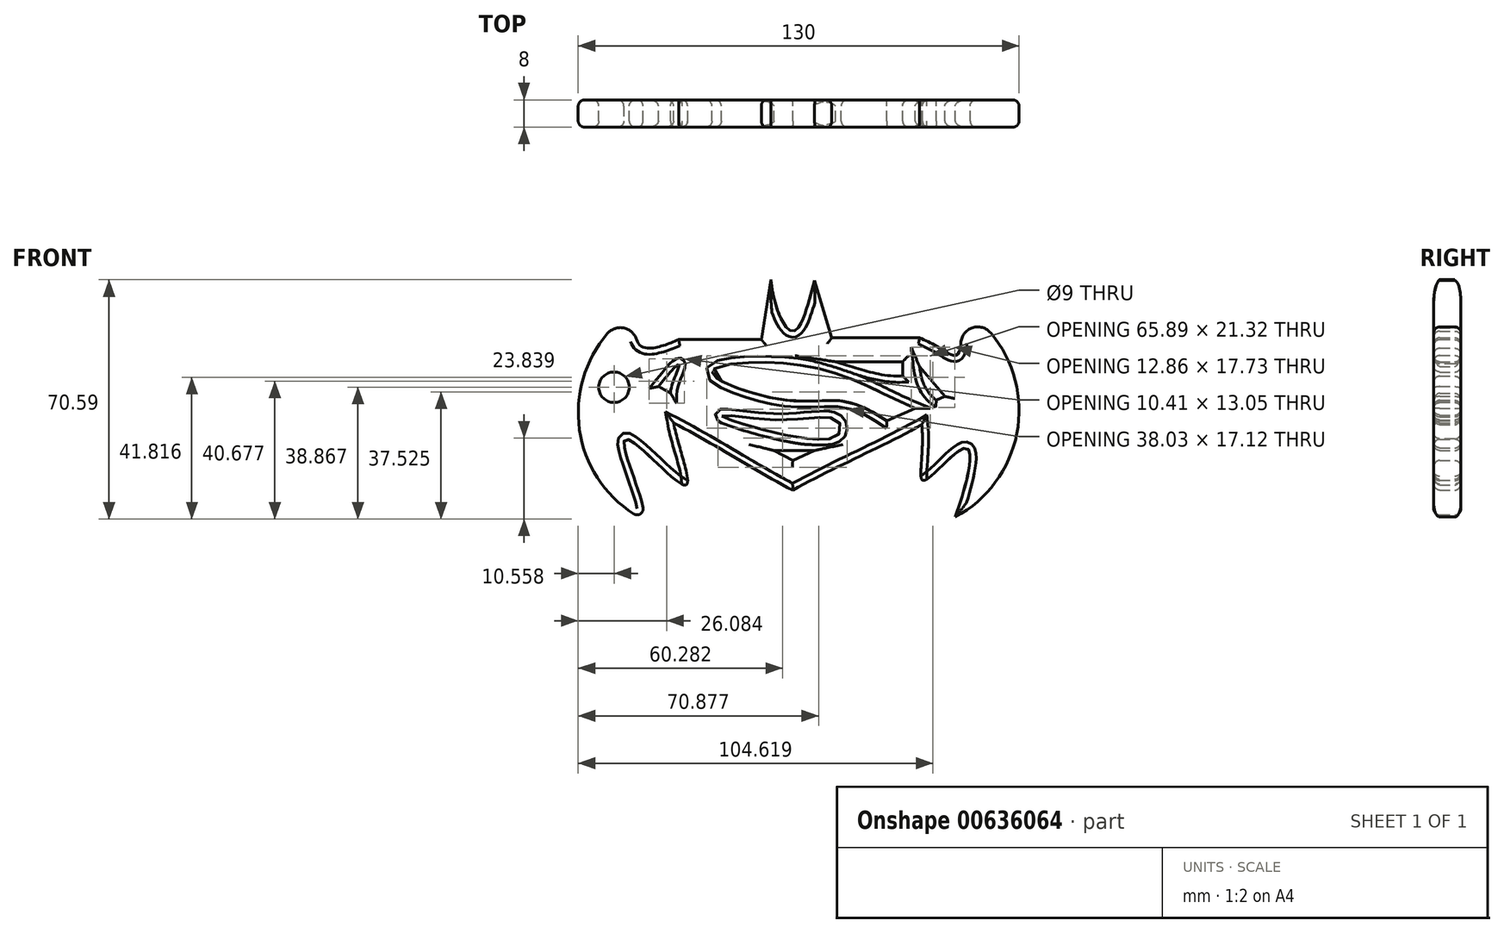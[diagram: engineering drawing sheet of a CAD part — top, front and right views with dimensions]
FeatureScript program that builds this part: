
annotation { "Feature Type Name" : "Feature", "Feature Type Description" : "" }
export const myFeature = defineFeature(function(context is Context, id is Id, definition is map)
    precondition{}
    {
        {
            var Q0;
            Q0=qCreatedBy(makeId("Front.planeOp"),FACE);
            var sketch = newSketch(context, id + "F0", { "sketchPlane" : qUnion([Q0])});
            skLineSegment(sketch, "E0", {"start": v(-12.91, 41.7) * mm, "end": v(-15.72, 24) * mm});
            skLineSegment(sketch, "E1", {"start": v(0, 41.41) * mm, "end": v(5.05, 24.57) * mm});
            skFitSpline(sketch, "E2", {"points": [v(-12.91, 41.7) * mm, v(-6.46, 26.53) * mm, v(0, 41.41) * mm], "startDerivative": vector(5.25, -48.76) * mm, "endDerivative": vector(12.88, 47.63) * mm});
            skLineSegment(sketch, "E3", {"start": v(-15.72, 24) * mm, "end": v(-40.11, 24) * mm});
            skLineSegment(sketch, "E4", {"start": v(5.05, 24.57) * mm, "end": v(30.98, 24.57) * mm});
            skFitSpline(sketch, "E5", {"points": [v(-40.11, 24) * mm, v(-51.3, 22.22) * mm, v(-50.91, 33.97) * mm], "startDerivative": vector(-39.59, -16.97) * mm, "endDerivative": vector(15.78, 44.08) * mm});
            skFitSpline(sketch, "E6", {"points": [v(30.98, 24.57) * mm, v(41.82, 19.47) * mm, v(41.48, 34.5) * mm], "startDerivative": vector(43.18, -18.5) * mm, "endDerivative": vector(-13.44, 48.11) * mm});
            skFitSpline(sketch, "E7", {"points": [v(41.48, -28.3) * mm, v(44.06, -8) * mm, v(32.34, -17.5) * mm, v(31.6, -1.1) * mm], "startDerivative": vector(35.63, 101) * mm, "endDerivative": vector(-8, 85.3) * mm});
            skFitSpline(sketch, "E8", {"points": [v(-50.91, -28.83) * mm, v(-50.91, -24.08) * mm, v(-55.7, -5.25) * mm, v(-38.31, -18.9) * mm, v(-41.58, -0.55) * mm], "startDerivative": vector(6.87, 19.6) * mm, "endDerivative": vector(-14.48, 80.7) * mm});
            skFitSpline(sketch, "E9", {"points": [v(-41.58, -0.55) * mm, v(-6.46, -20.38) * mm], "startDerivative": vector(37.07, -19.28) * mm, "endDerivative": vector(37.07, -19.28) * mm});
            skFitSpline(sketch, "E10", {"points": [v(31.6, -1.1) * mm, v(-6.46, -20.38) * mm], "startDerivative": vector(-37.45, -20.69) * mm, "endDerivative": vector(-37.45, -20.69) * mm});
            skLineSegment(sketch, "E11", {"start": v(-6.46, -15.44) * mm, "end": v(41.82, 6.41) * mm});
            skLineSegment(sketch, "E12", {"start": v(41.82, 6.41) * mm, "end": v(30.98, 21.66) * mm});
            skLineSegment(sketch, "E13", {"start": v(30.98, 21.66) * mm, "end": v(-40.11, 21.2) * mm});
            skLineSegment(sketch, "E14", {"start": v(-40.11, 21.2) * mm, "end": v(-51.3, 8.73) * mm});
            skLineSegment(sketch, "E15", {"start": v(-51.3, 8.73) * mm, "end": v(-6.46, -15.44) * mm});
            skArc(sketch, "E16", {"start": v(-50.91, 33.97) * mm, "mid": v(-69.72, 2.57) * mm, "end": v(-50.91, -28.83) * mm});
            skArc(sketch, "E17", {"start": v(41.48, -28.3) * mm, "mid": v(60.28, 3.1) * mm, "end": v(41.48, 34.5) * mm});
            skLineSegment(sketch, "E18", {"start": v(-6.46, -11.62) * mm, "end": v(0, -8.7) * mm});
            skLineSegment(sketch, "E19", {"start": v(0, -8.7) * mm, "end": v(-12.03, -8.7) * mm});
            skLineSegment(sketch, "E20", {"start": v(-12.03, -8.7) * mm, "end": v(-6.46, -11.62) * mm});
            skFitSpline(sketch, "E21", {"points": [v(-27.4, 1.5) * mm, v(-10.6, 0.35) * mm, v(6.93, 0) * mm, v(5.75, -4.85) * mm, v(-27.4, 1.5) * mm]});
            skLineSegment(sketch, "E22", {"start": v(-46.08, 10.16) * mm, "end": v(-42.51, 8.24) * mm});
            skLineSegment(sketch, "E23", {"start": v(35.92, 6.14) * mm, "end": v(38.41, 7.27) * mm});
            skLineSegment(sketch, "E24", {"start": v(38.41, 7.27) * mm, "end": v(30.96, 16.07) * mm});
            skFitSpline(sketch, "E25", {"points": [v(30.96, 16.07) * mm, v(35.92, 6.14) * mm], "startDerivative": vector(1.42, -12.05) * mm, "endDerivative": vector(10.63, -8.5) * mm});
            skLineSegment(sketch, "E26", {"start": v(25.93, 17.49) * mm, "end": v(25.96, 13.23) * mm});
            skLineSegment(sketch, "E27", {"start": v(25.96, 13.23) * mm, "end": v(25.93, 17.49) * mm});
            skLineSegment(sketch, "E28", {"start": v(6.14, 17.49) * mm, "end": v(25.93, 17.49) * mm});
            skFitSpline(sketch, "E29", {"points": [v(6.14, 17.49) * mm, v(25.96, 13.23) * mm], "startDerivative": vector(18.43, -5.67) * mm, "endDerivative": vector(19.75, 0.7) * mm});
            skLineSegment(sketch, "E30", {"start": v(21.34, 0) * mm, "end": v(29.64, 3.76) * mm});
            skFitSpline(sketch, "E31", {"points": [v(29.64, 3.76) * mm, v(-2.9, 16.3) * mm, v(-30.27, 14.52) * mm, v(-9.16, 6.26) * mm, v(8.78, 5.78) * mm, v(16.3, 3.13) * mm, v(21.34, 0) * mm], "startDerivative": vector(-155.46, 66.73) * mm, "endDerivative": vector(157.37, -97.92) * mm});
            skFitSpline(sketch, "E32", {"points": [v(-46.08, 10.16) * mm, v(-39.94, 16.69) * mm, v(-42.51, 8.24) * mm], "startDerivative": vector(16.59, 20.52) * mm, "endDerivative": vector(-0.25, -15.84) * mm});
            skCircle(sketch, "E33", {"center": v(-59.16, 9.97) * mm, "radius": 4.5 * mm});
            skSolve(sketch);
        }
        {
            var Q0;
            Q0=makeQuery(id+"F0.imprint","IMPRINT",FACE,{"disambiguationData":[TD([[makeQuery(id+"F0.imprint","IMPRINT",EDGE,{"derivedFrom":sQuery(id+"F0.wireOp",EDGE,"E11")}),1.0]])]});
            var Q1;
            Q1=makeQuery(id+"F0.imprint","IMPRINT",FACE,{"disambiguationData":[TD([[makeQuery(id+"F0.imprint","IMPRINT",EDGE,{"derivedFrom":sQuery(id+"F0.wireOp",EDGE,"E0")}),1.0]])]});
            extrude(context, id + "F1", {"entities" : qUnion([Q0, Q1]), "depth" : 8 * mm});
        }
        {
            var Q0;
            Q0=makeQuery(id+"F1.opExtrude","SWEPT_EDGE",EDGE,{"disambiguationData":[OSD([sQuery(id+"F0.wireOp",EDGE,"E8"),sQuery(id+"F0.wireOp",EDGE,"E16")])]});
            var Q1;
            Q1=makeQuery(id+"F1.opExtrude","CAP_FACE",FACE,{"disambiguationData":[OSD([sQuery(id+"F0.wireOp",EDGE,"E0"),sQuery(id+"F0.wireOp",EDGE,"E1"),sQuery(id+"F0.wireOp",EDGE,"E2"),sQuery(id+"F0.wireOp",EDGE,"E3"),sQuery(id+"F0.wireOp",EDGE,"E4"),sQuery(id+"F0.wireOp",EDGE,"E5"),sQuery(id+"F0.wireOp",EDGE,"E6"),sQuery(id+"F0.wireOp",EDGE,"E7"),sQuery(id+"F0.wireOp",EDGE,"E8"),sQuery(id+"F0.wireOp",EDGE,"E9"),sQuery(id+"F0.wireOp",EDGE,"E10"),sQuery(id+"F0.wireOp",EDGE,"E16"),sQuery(id+"F0.wireOp",EDGE,"E17"),sQuery(id+"F0.wireOp",EDGE,"E18"),sQuery(id+"F0.wireOp",EDGE,"E19"),sQuery(id+"F0.wireOp",EDGE,"E20"),sQuery(id+"F0.wireOp",EDGE,"E21"),sQuery(id+"F0.wireOp",EDGE,"E22"),sQuery(id+"F0.wireOp",EDGE,"E23"),sQuery(id+"F0.wireOp",EDGE,"E24"),sQuery(id+"F0.wireOp",EDGE,"E25"),sQuery(id+"F0.wireOp",EDGE,"E27"),sQuery(id+"F0.wireOp",EDGE,"E28"),sQuery(id+"F0.wireOp",EDGE,"E29"),sQuery(id+"F0.wireOp",EDGE,"E30"),sQuery(id+"F0.wireOp",EDGE,"E31"),sQuery(id+"F0.wireOp",EDGE,"E32"),sQuery(id+"F0.wireOp",EDGE,"E33")])],"isStart":true});
            var Q2;
            Q2=makeQuery(id+"F1.opExtrude","CAP_FACE",FACE,{"disambiguationData":[OSD([sQuery(id+"F0.wireOp",EDGE,"E0"),sQuery(id+"F0.wireOp",EDGE,"E1"),sQuery(id+"F0.wireOp",EDGE,"E2"),sQuery(id+"F0.wireOp",EDGE,"E3"),sQuery(id+"F0.wireOp",EDGE,"E4"),sQuery(id+"F0.wireOp",EDGE,"E5"),sQuery(id+"F0.wireOp",EDGE,"E6"),sQuery(id+"F0.wireOp",EDGE,"E7"),sQuery(id+"F0.wireOp",EDGE,"E8"),sQuery(id+"F0.wireOp",EDGE,"E9"),sQuery(id+"F0.wireOp",EDGE,"E10"),sQuery(id+"F0.wireOp",EDGE,"E16"),sQuery(id+"F0.wireOp",EDGE,"E17"),sQuery(id+"F0.wireOp",EDGE,"E18"),sQuery(id+"F0.wireOp",EDGE,"E19"),sQuery(id+"F0.wireOp",EDGE,"E20"),sQuery(id+"F0.wireOp",EDGE,"E21"),sQuery(id+"F0.wireOp",EDGE,"E22"),sQuery(id+"F0.wireOp",EDGE,"E23"),sQuery(id+"F0.wireOp",EDGE,"E24"),sQuery(id+"F0.wireOp",EDGE,"E25"),sQuery(id+"F0.wireOp",EDGE,"E27"),sQuery(id+"F0.wireOp",EDGE,"E28"),sQuery(id+"F0.wireOp",EDGE,"E29"),sQuery(id+"F0.wireOp",EDGE,"E30"),sQuery(id+"F0.wireOp",EDGE,"E31"),sQuery(id+"F0.wireOp",EDGE,"E32"),sQuery(id+"F0.wireOp",EDGE,"E33")])],"isStart":false});
            var Q3;
            Q3=makeQuery(id+"F1.opExtrude","CAP_EDGE",EDGE,{"disambiguationData":[OSD([sQuery(id+"F0.wireOp",EDGE,"E8")])],"isStart":false});
            var Q4;
            Q4=makeQuery(id+"F1.opExtrude","CAP_EDGE",EDGE,{"disambiguationData":[OSD([sQuery(id+"F0.wireOp",EDGE,"E5")])],"isStart":false});
            var Q5;
            Q5=makeQuery(id+"F1.opExtrude","CAP_EDGE",EDGE,{"disambiguationData":[OSD([sQuery(id+"F0.wireOp",EDGE,"E16")])],"isStart":true});
            var Q6;
            Q6=makeQuery(id+"F1.opExtrude","CAP_EDGE",EDGE,{"disambiguationData":[OSD([sQuery(id+"F0.wireOp",EDGE,"E5")])],"isStart":true});
            fillet(context, id + "F2", {"entities" : qUnion([Q0, Q1, Q2, Q3, Q4, Q5, Q6]), "radius" : 1.8 * mm, "tangentPropagation" : true, "allowEdgeOverflow" : false});
        }
        {
            var Q0;
            Q0=makeQuery(id+"F2.opFillet","BLEND_EDGE",EDGE,{"blendedFrom":[makeQuery(id+"F1.opExtrude","CAP_EDGE",EDGE,{"disambiguationData":[OSD([sQuery(id+"F0.wireOp",EDGE,"E5")])],"isStart":false}),makeQuery(id+"F1.opExtrude","CAP_EDGE",EDGE,{"disambiguationData":[OSD([sQuery(id+"F0.wireOp",EDGE,"E16")])],"isStart":false})],"blendedInto":[]});
            var Q1;
            Q1=makeQuery(id+"F1.opExtrude","CAP_FACE",FACE,{"disambiguationData":[OSD([sQuery(id+"F0.wireOp",EDGE,"E0"),sQuery(id+"F0.wireOp",EDGE,"E1"),sQuery(id+"F0.wireOp",EDGE,"E2"),sQuery(id+"F0.wireOp",EDGE,"E3"),sQuery(id+"F0.wireOp",EDGE,"E4"),sQuery(id+"F0.wireOp",EDGE,"E5"),sQuery(id+"F0.wireOp",EDGE,"E6"),sQuery(id+"F0.wireOp",EDGE,"E7"),sQuery(id+"F0.wireOp",EDGE,"E8"),sQuery(id+"F0.wireOp",EDGE,"E9"),sQuery(id+"F0.wireOp",EDGE,"E10"),sQuery(id+"F0.wireOp",EDGE,"E16"),sQuery(id+"F0.wireOp",EDGE,"E17"),sQuery(id+"F0.wireOp",EDGE,"E18"),sQuery(id+"F0.wireOp",EDGE,"E19"),sQuery(id+"F0.wireOp",EDGE,"E20"),sQuery(id+"F0.wireOp",EDGE,"E21"),sQuery(id+"F0.wireOp",EDGE,"E22"),sQuery(id+"F0.wireOp",EDGE,"E23"),sQuery(id+"F0.wireOp",EDGE,"E24"),sQuery(id+"F0.wireOp",EDGE,"E25"),sQuery(id+"F0.wireOp",EDGE,"E27"),sQuery(id+"F0.wireOp",EDGE,"E28"),sQuery(id+"F0.wireOp",EDGE,"E29"),sQuery(id+"F0.wireOp",EDGE,"E30"),sQuery(id+"F0.wireOp",EDGE,"E31"),sQuery(id+"F0.wireOp",EDGE,"E32"),sQuery(id+"F0.wireOp",EDGE,"E33")])],"isStart":false});
            fillet(context, id + "F3", {"entities" : qUnion([Q0, Q1]), "radius" : 5 * mm, "tangentPropagation" : true, "allowEdgeOverflow" : false});
        }
        {
            var Q0;
            Q0=makeQuery(id+"F2.opFillet","BLEND_EDGE",EDGE,{"blendedFrom":[makeQuery(id+"F1.opExtrude","CAP_EDGE",EDGE,{"disambiguationData":[OSD([sQuery(id+"F0.wireOp",EDGE,"E6")])],"isStart":false}),makeQuery(id+"F1.opExtrude","CAP_EDGE",EDGE,{"disambiguationData":[OSD([sQuery(id+"F0.wireOp",EDGE,"E17")])],"isStart":false})],"blendedInto":[]});
            var Q1;
            {var subQ0=sQuery(id+"F0.wireOp",EDGE,"E6");Q1=makeQuery(id+"F2.opFillet","BLEND_EDGE",EDGE,{"blendedFrom":[makeQuery(id+"F1.opExtrude","CAP_EDGE",EDGE,{"disambiguationData":[OSD([subQ0])],"isStart":false}),makeQuery(id+"F1.opExtrude","CAP_FACE",FACE,{"disambiguationData":[OSD([sQuery(id+"F0.wireOp",EDGE,"E0"),sQuery(id+"F0.wireOp",EDGE,"E1"),sQuery(id+"F0.wireOp",EDGE,"E2"),sQuery(id+"F0.wireOp",EDGE,"E3"),sQuery(id+"F0.wireOp",EDGE,"E4"),sQuery(id+"F0.wireOp",EDGE,"E5"),subQ0,sQuery(id+"F0.wireOp",EDGE,"E7"),sQuery(id+"F0.wireOp",EDGE,"E8"),sQuery(id+"F0.wireOp",EDGE,"E9"),sQuery(id+"F0.wireOp",EDGE,"E10"),sQuery(id+"F0.wireOp",EDGE,"E16"),sQuery(id+"F0.wireOp",EDGE,"E17"),sQuery(id+"F0.wireOp",EDGE,"E18"),sQuery(id+"F0.wireOp",EDGE,"E19"),sQuery(id+"F0.wireOp",EDGE,"E20"),sQuery(id+"F0.wireOp",EDGE,"E21"),sQuery(id+"F0.wireOp",EDGE,"E22"),sQuery(id+"F0.wireOp",EDGE,"E23"),sQuery(id+"F0.wireOp",EDGE,"E24"),sQuery(id+"F0.wireOp",EDGE,"E25"),sQuery(id+"F0.wireOp",EDGE,"E27"),sQuery(id+"F0.wireOp",EDGE,"E28"),sQuery(id+"F0.wireOp",EDGE,"E29"),sQuery(id+"F0.wireOp",EDGE,"E30"),sQuery(id+"F0.wireOp",EDGE,"E31"),sQuery(id+"F0.wireOp",EDGE,"E32"),sQuery(id+"F0.wireOp",EDGE,"E33")])],"isStart":false})],"blendedInto":[makeQuery(id+"F1.opExtrude","CAP_FACE",FACE,{"disambiguationData":[OSD([sQuery(id+"F0.wireOp",EDGE,"E0"),sQuery(id+"F0.wireOp",EDGE,"E1"),sQuery(id+"F0.wireOp",EDGE,"E2"),sQuery(id+"F0.wireOp",EDGE,"E3"),sQuery(id+"F0.wireOp",EDGE,"E4"),sQuery(id+"F0.wireOp",EDGE,"E5"),subQ0,sQuery(id+"F0.wireOp",EDGE,"E7"),sQuery(id+"F0.wireOp",EDGE,"E8"),sQuery(id+"F0.wireOp",EDGE,"E9"),sQuery(id+"F0.wireOp",EDGE,"E10"),sQuery(id+"F0.wireOp",EDGE,"E16"),sQuery(id+"F0.wireOp",EDGE,"E17"),sQuery(id+"F0.wireOp",EDGE,"E18"),sQuery(id+"F0.wireOp",EDGE,"E19"),sQuery(id+"F0.wireOp",EDGE,"E20"),sQuery(id+"F0.wireOp",EDGE,"E21"),sQuery(id+"F0.wireOp",EDGE,"E22"),sQuery(id+"F0.wireOp",EDGE,"E23"),sQuery(id+"F0.wireOp",EDGE,"E24"),sQuery(id+"F0.wireOp",EDGE,"E25"),sQuery(id+"F0.wireOp",EDGE,"E27"),sQuery(id+"F0.wireOp",EDGE,"E28"),sQuery(id+"F0.wireOp",EDGE,"E29"),sQuery(id+"F0.wireOp",EDGE,"E30"),sQuery(id+"F0.wireOp",EDGE,"E31"),sQuery(id+"F0.wireOp",EDGE,"E32"),sQuery(id+"F0.wireOp",EDGE,"E33")])],"isStart":false})]});}
            fillet(context, id + "F4", {"entities" : qUnion([Q0, Q1]), "radius" : 5 * mm, "tangentPropagation" : true, "allowEdgeOverflow" : false});
        }
    });
